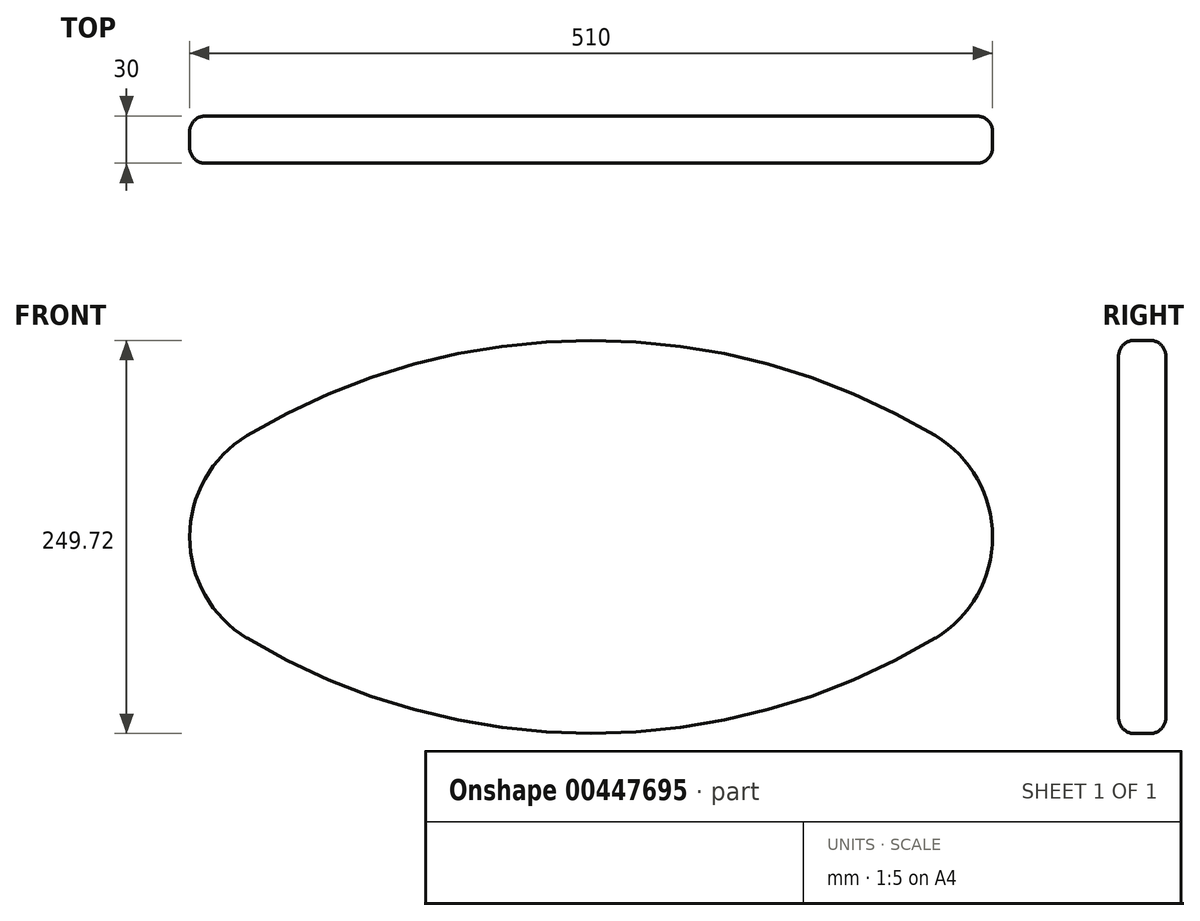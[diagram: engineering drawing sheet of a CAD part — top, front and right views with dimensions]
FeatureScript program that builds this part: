
annotation { "Feature Type Name" : "Feature", "Feature Type Description" : "" }
export const myFeature = defineFeature(function(context is Context, id is Id, definition is map)
    precondition{}
    {
        {
            var Q0;
            Q0=qCreatedBy(makeId("Front.planeOp"),FACE);
            var sketch = newSketch(context, id + "F0", { "sketchPlane" : qUnion([Q0])});
            skArc(sketch, "E0", {"start": v(-218.59, 64.31) * mm, "mid": v(-255, 0) * mm, "end": v(-218.59, -64.31) * mm});
            skArc(sketch, "E1", {"start": v(218.59, -64.31) * mm, "mid": v(255, 0) * mm, "end": v(218.59, 64.31) * mm});
            skArc(sketch, "E2", {"start": v(-218.59, -64.31) * mm, "mid": v(0, -124.86) * mm, "end": v(218.59, -64.31) * mm});
            skArc(sketch, "E3.trimOffspring", {"start": v(218.59, 64.31) * mm, "mid": v(0, 124.86) * mm, "end": v(-218.59, 64.31) * mm});
            skSolve(sketch);
        }
        {
            var Q0;
            Q0 = qSketchRegion(id + "F0", true);
            extrude(context, id + "F1", {"entities" : qUnion([Q0]), "depth" : 30 * mm});
        }
        {
            var Q0;
            Q0=makeQuery(id+"F1.opExtrude","CAP_EDGE",EDGE,{"disambiguationData":[OSD([sQuery(id+"F0.wireOp",EDGE,"E2")])],"isStart":false});
            var Q1;
            Q1=makeQuery(id+"F1.opExtrude","CAP_EDGE",EDGE,{"disambiguationData":[OSD([sQuery(id+"F0.wireOp",EDGE,"E2")])],"isStart":true});
            fillet(context, id + "F2", {"entities" : qUnion([Q0, Q1]), "radius" : 10 * mm, "tangentPropagation" : true, "allowEdgeOverflow" : false});
        }
    });
